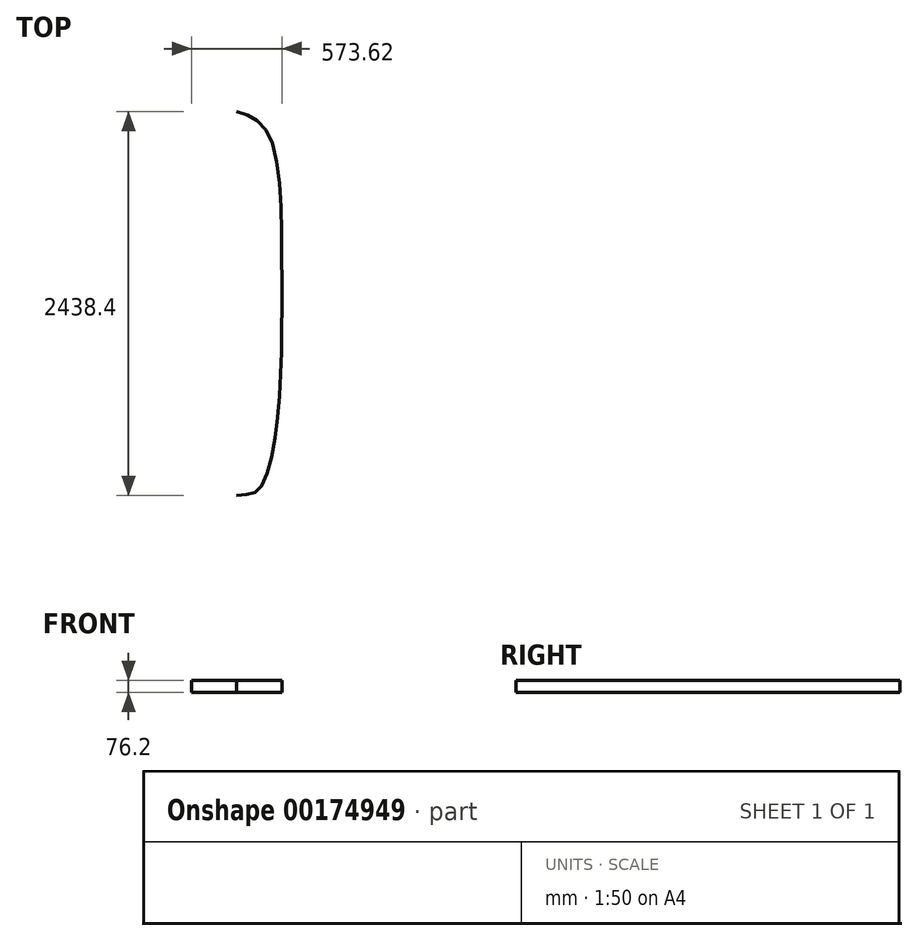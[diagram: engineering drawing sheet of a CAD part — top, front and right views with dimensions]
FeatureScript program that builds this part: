
annotation { "Feature Type Name" : "Feature", "Feature Type Description" : "" }
export const myFeature = defineFeature(function(context is Context, id is Id, definition is map)
    precondition{}
    {
        {
            var Q0;
            Q0=qCreatedBy(makeId("Top.planeOp"),FACE);
            var sketch = newSketch(context, id + "F0", { "sketchPlane" : qUnion([Q0])});
            skPoint(sketch, "E0.middle", {"position": v(0, 0) * mm});
            skFitSpline(sketch, "E1", {"points": [v(0, 1219.2) * mm, v(-196.28, 1084.75) * mm, v(-286.28, 232.27) * mm, v(-263.87, -688.32) * mm, v(-139.24, -1182.45) * mm, v(0, -1219.2) * mm], "startDerivative": vector(-1553.7, -418.7) * mm, "endDerivative": vector(1621.5, -167) * mm});
            skLineSegment(sketch, "E2", {"start": v(0, 1219.2) * mm, "end": v(0, -1219.2) * mm, "construction": true});
            skFitSpline(sketch, "E3.MirrorCS", {"points": [v(0, 1219.2) * mm, v(196.28, 1084.75) * mm, v(286.28, 232.27) * mm, v(263.87, -688.32) * mm, v(139.24, -1182.45) * mm, v(0, -1219.2) * mm], "startDerivative": vector(1553.7, -418.7) * mm, "endDerivative": vector(-1621.5, -167) * mm});
            skSolve(sketch);
        }
        {
            var Q0;
            Q0=makeQuery(id+"F0.imprint","IMPRINT",FACE,{"disambiguationData":[TD([[makeQuery(id+"F0.imprint","IMPRINT",EDGE,{"derivedFrom":sQuery(id+"F0.wireOp",EDGE,"E1")}),1.0]])]});
            extrude(context, id + "F1", {"entities" : qUnion([Q0]), "depth" : 76.2 * mm, "offsetDistance" : 25.4 * mm});
        }
    });
